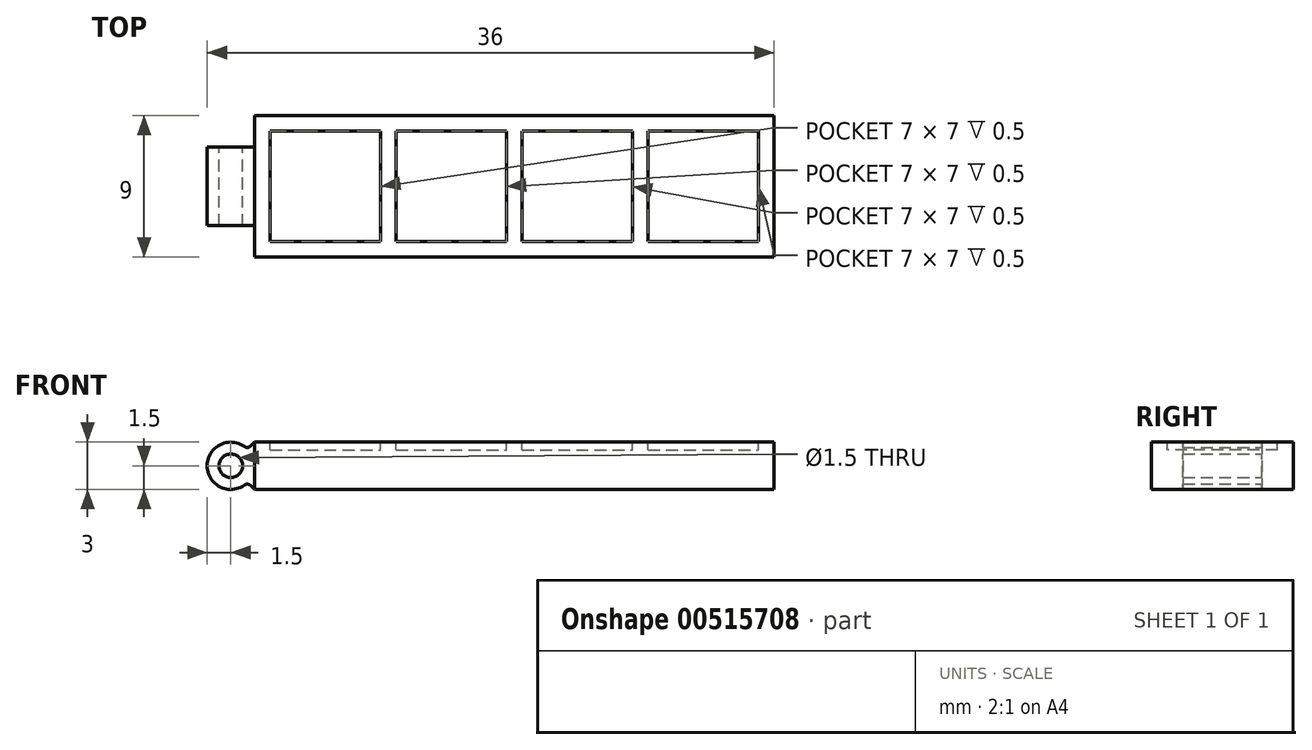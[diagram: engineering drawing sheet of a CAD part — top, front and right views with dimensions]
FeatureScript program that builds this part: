
annotation { "Feature Type Name" : "Feature", "Feature Type Description" : "" }
export const myFeature = defineFeature(function(context is Context, id is Id, definition is map)
    precondition{}
    {
        {
            var Q0;
            Q0=qCreatedBy(makeId("Front.planeOp"),FACE);
            var sketch = newSketch(context, id + "F0", { "sketchPlane" : qUnion([Q0])});
            skLineSegment(sketch, "E0.bottom", {"start": v(1.5, 3) * mm, "end": v(34.5, 3) * mm});
            skLineSegment(sketch, "E0.top", {"start": v(1.5, 0) * mm, "end": v(34.5, 0) * mm});
            skLineSegment(sketch, "E0.left", {"start": v(1.5, 3) * mm, "end": v(1.5, 0) * mm});
            skLineSegment(sketch, "E0.right", {"start": v(34.5, 3) * mm, "end": v(34.5, 0) * mm});
            skLineSegment(sketch, "E1", {"start": v(-13.71, 0) * mm, "end": v(-1.5, 0) * mm, "construction": true});
            skCircle(sketch, "E2", {"center": v(0, 1.5) * mm, "radius": 1.5 * mm});
            skCircle(sketch, "E3", {"center": v(0, 1.5) * mm, "radius": 0.75 * mm});
            skLineSegment(sketch, "E4", {"start": v(0, 1.6) * mm, "end": v(0, 6.8) * mm, "construction": true});
            skLineSegment(sketch, "E5", {"start": v(0, 1.5) * mm, "end": v(1.06, 0.44) * mm, "construction": true});
            skPoint(sketch, "E6.MirrorCS.start.orphan", {"position": v(-1.06, 0.44) * mm});
            skLineSegment(sketch, "E7.trimOffspring", {"start": v(1.5, 0) * mm, "end": v(15.8, 0) * mm, "construction": true});
            skPoint(sketch, "E8.end.orphan", {"position": v(1.5, 0) * mm});
            skLineSegment(sketch, "E9", {"start": v(-1.82, 1.5) * mm, "end": v(2.2, 1.5) * mm, "construction": true});
            skPoint(sketch, "E9.endSnap0", {"position": v(1.5, 1.5) * mm});
            skLineSegment(sketch, "E10", {"start": v(1.06, 0.44) * mm, "end": v(1.5, 0) * mm});
            skLineSegment(sketch, "E11.MirrorCS", {"start": v(1.06, 2.56) * mm, "end": v(1.5, 3) * mm});
            skSolve(sketch);
        }
        {
            var Q0;
            {var subQ3=sQuery(id+"F0.wireOp",EDGE,"E0.bottom");Q0=makeQuery(id+"F0.imprint","IMPRINT",FACE,{"disambiguationData":[TD([[makeQuery(id+"F0.imprint","IMPRINT",EDGE,{"derivedFrom":subQ3}),-1.0]])]});}
            extrude(context, id + "F1", {"entities" : qUnion([Q0]), "endBound" : BoundingType.SYMMETRIC, "depth" : (7 + 1 * 2) * mm, "offsetDistance" : 25 * mm});
        }
        {
            var Q0;
            {var subQ0=sQuery(id+"F0.wireOp",EDGE,"E11.MirrorCS");Q0=makeQuery(id+"F0.imprint","IMPRINT",FACE,{"disambiguationData":[TD([[makeQuery(id+"F0.imprint","IMPRINT",EDGE,{"derivedFrom":subQ0}),-1.0]])]});}
            var Q1;
            {var subQ0=sQuery(id+"F0.wireOp",EDGE,"E10");Q1=makeQuery(id+"F0.imprint","IMPRINT",FACE,{"disambiguationData":[TD([[makeQuery(id+"F0.imprint","IMPRINT",EDGE,{"derivedFrom":subQ0}),1.0]])]});}
            var Q2;
            Q2=makeQuery(id+"F0.imprint","IMPRINT",FACE,{"disambiguationData":[TD([[makeQuery(id+"F0.imprint","IMPRINT",EDGE,{"derivedFrom":sQuery(id+"F0.wireOp",EDGE,"E3")}),-1.0]])]});
            extrude(context, id + "F2", {"entities" : qUnion([Q0, Q1, Q2]), "operationType" : NewBodyOperationType.ADD, "endBound" : BoundingType.SYMMETRIC, "depth" : 5 * mm, "offsetDistance" : 25 * mm});
        }
        {
            var Q0;
            Q0=makeQuery(id+"F1.opExtrude","SWEPT_FACE",FACE,{"disambiguationData":[OSD([sQuery(id+"F0.wireOp",EDGE,"E0.bottom")])]});
            var sketch = newSketch(context, id + "F3", { "sketchPlane" : qUnion([Q0])});
            skLineSegment(sketch, "E12.bottom", {"start": v(26.5, 3.5) * mm, "end": v(33.5, 3.5) * mm});
            skLineSegment(sketch, "E12.top", {"start": v(26.5, -3.5) * mm, "end": v(33.5, -3.5) * mm});
            skLineSegment(sketch, "E12.left", {"start": v(26.5, 3.5) * mm, "end": v(26.5, -3.5) * mm});
            skLineSegment(sketch, "E12.right", {"start": v(33.5, 3.5) * mm, "end": v(33.5, -3.5) * mm});
            skLineSegment(sketch, "E13.0", {"start": v(-13.71, 0) * mm, "end": v(-1.5, 0) * mm, "construction": true});
            skLineSegment(sketch, "E14.1.0.0", {"start": v(18.5, 3.5) * mm, "end": v(25.5, 3.5) * mm});
            skLineSegment(sketch, "E14.1.0.1", {"start": v(18.5, 3.5) * mm, "end": v(18.5, -3.5) * mm});
            skLineSegment(sketch, "E14.1.0.2", {"start": v(18.5, -3.5) * mm, "end": v(25.5, -3.5) * mm});
            skLineSegment(sketch, "E14.1.0.3", {"start": v(25.5, 3.5) * mm, "end": v(25.5, -3.5) * mm});
            skLineSegment(sketch, "E14.2.0.0", {"start": v(10.5, 3.5) * mm, "end": v(17.5, 3.5) * mm});
            skLineSegment(sketch, "E14.2.0.1", {"start": v(10.5, 3.5) * mm, "end": v(10.5, -3.5) * mm});
            skLineSegment(sketch, "E14.2.0.2", {"start": v(10.5, -3.5) * mm, "end": v(17.5, -3.5) * mm});
            skLineSegment(sketch, "E14.2.0.3", {"start": v(17.5, 3.5) * mm, "end": v(17.5, -3.5) * mm});
            skLineSegment(sketch, "E14.3.0.0", {"start": v(2.5, 3.5) * mm, "end": v(9.5, 3.5) * mm});
            skLineSegment(sketch, "E14.3.0.1", {"start": v(2.5, 3.5) * mm, "end": v(2.5, -3.5) * mm});
            skLineSegment(sketch, "E14.3.0.2", {"start": v(2.5, -3.5) * mm, "end": v(9.5, -3.5) * mm});
            skLineSegment(sketch, "E14.3.0.3", {"start": v(9.5, 3.5) * mm, "end": v(9.5, -3.5) * mm});
            skLineSegment(sketch, "E14.direction1", {"start": v(26.5, 3.5) * mm, "end": v(18.5, 3.5) * mm, "construction": true});
            skSolve(sketch);
        }
        {
            var Q0;
            Q0=makeQuery(id+"F3.imprint","IMPRINT",FACE,{"disambiguationData":[TD([[makeQuery(id+"F3.imprint","IMPRINT",EDGE,{"derivedFrom":sQuery(id+"F3.wireOp",EDGE,"E12.bottom")}),-1.0]])]});
            var Q1;
            Q1=makeQuery(id+"F3.imprint","IMPRINT",FACE,{"disambiguationData":[TD([[makeQuery(id+"F3.imprint","IMPRINT",EDGE,{"derivedFrom":sQuery(id+"F3.wireOp",EDGE,"E14.1.0.0")}),-1.0]])]});
            var Q2;
            Q2=makeQuery(id+"F3.imprint","IMPRINT",FACE,{"disambiguationData":[TD([[makeQuery(id+"F3.imprint","IMPRINT",EDGE,{"derivedFrom":sQuery(id+"F3.wireOp",EDGE,"E14.2.0.0")}),-1.0]])]});
            var Q3;
            Q3=makeQuery(id+"F3.imprint","IMPRINT",FACE,{"disambiguationData":[TD([[makeQuery(id+"F3.imprint","IMPRINT",EDGE,{"derivedFrom":sQuery(id+"F3.wireOp",EDGE,"E14.3.0.0")}),-1.0]])]});
            extrude(context, id + "F4", {"entities" : qUnion([Q0, Q1, Q2, Q3]), "operationType" : NewBodyOperationType.REMOVE, "oppositeDirection" : true, "depth" : .5 * mm, "offsetDistance" : 25 * mm});
        }
        {
            var Q0;
            Q0=makeQuery(id+"F3.imprint","IMPRINT",FACE,{"disambiguationData":[TD([[makeQuery(id+"F3.imprint","IMPRINT",EDGE,{"derivedFrom":sQuery(id+"F3.wireOp",EDGE,"E14.3.0.0")}),-1.0]])]});
            var Q1;
            Q1=makeQuery(id+"F3.imprint","IMPRINT",FACE,{"disambiguationData":[TD([[makeQuery(id+"F3.imprint","IMPRINT",EDGE,{"derivedFrom":sQuery(id+"F3.wireOp",EDGE,"E14.2.0.0")}),-1.0]])]});
            var Q2;
            Q2=makeQuery(id+"F3.imprint","IMPRINT",FACE,{"disambiguationData":[TD([[makeQuery(id+"F3.imprint","IMPRINT",EDGE,{"derivedFrom":sQuery(id+"F3.wireOp",EDGE,"E14.1.0.0")}),-1.0]])]});
            var Q3;
            Q3=makeQuery(id+"F3.imprint","IMPRINT",FACE,{"disambiguationData":[TD([[makeQuery(id+"F3.imprint","IMPRINT",EDGE,{"derivedFrom":sQuery(id+"F3.wireOp",EDGE,"E12.bottom")}),-1.0]])]});
            extrude(context, id + "F5", {"entities" : qUnion([Q0, Q1, Q2, Q3]), "oppositeDirection" : true, "depth" : .5 * mm, "offsetDistance" : 25 * mm});
        }
        {
            var Q0;
            Q0=makeQuery(id+"F2.opExtrude","SWEPT_EDGE",EDGE,{"disambiguationData":[OSD([sQuery(id+"F0.wireOp",EDGE,"E2"),sQuery(id+"F0.wireOp",EDGE,"E11.MirrorCS")])]});
            var Q1;
            Q1=makeQuery(id+"F2.opExtrude","SWEPT_EDGE",EDGE,{"disambiguationData":[OSD([sQuery(id+"F0.wireOp",EDGE,"E2"),sQuery(id+"F0.wireOp",EDGE,"E10")])]});
            fillet(context, id + "F6", {"entities" : qUnion([Q0, Q1]), "radius" : .3 * mm, "tangentPropagation" : true, "allowEdgeOverflow" : false});
        }
    });
